# Revit family: Toilet-Floor_Mount-KOHLER-Primary-K-96064
name_source: partatom
category: Plumbing Fixtures
revit_build: Autodesk Revit 2015 (Build: 20140606_1530(x64)
units: mm (PartAtom-declared; Revit-internal decimal feet)

## types (2) — shared parameters
ADA Compliant = Yes
Assembly Code = D2010100
CW Connection = Yes
Cold Water Inlet = Cold Water Inlet
Date Modified = 03/21/2018
Default Elevation = 0"
Finish = Kohler-Vitreous_China-0-White
Flow Rate = 25 GPM
Flush Rate = 1.6 GPF
HW Connection = No
Height = 12 5/16"
Hot Water Inlet = Hot Water Inlet
Length = 24 7/16"
Manufacturer = KOHLER Co.
MasterFormat 1995 = 15410
MasterFormat 2004 = 22.41.13
Material = Vitreous China
Pressure = 80.00 psi
Product Documentation Link = http://www.us.kohler.com
Product Name = Primary
Product Page URL = http://www.us.kohler.com
Rough-In = 10"
URL = https://www.us.kohler.com
Vent Connection = No
Waste Connection = Yes
Waste Water Outlet = Waste Water Outlet
Width = 14 7/16"

## per-type parameters (varying)
| type | Description | Model | Type |
| Flushometer Bowl, 0-White | Elongated floor-mount flushometer bowl | K-96064-0 | 1 |
| Bowl With Antimicrobial Finish, 0-White | Elongated floor-mount flushometer bowl, Antimicrobial finish | K-96064-SS-0 | 2 |

## geometry (parser evidence)
native form markers: Sweep x5
no freeform markers — native parametric forms only
